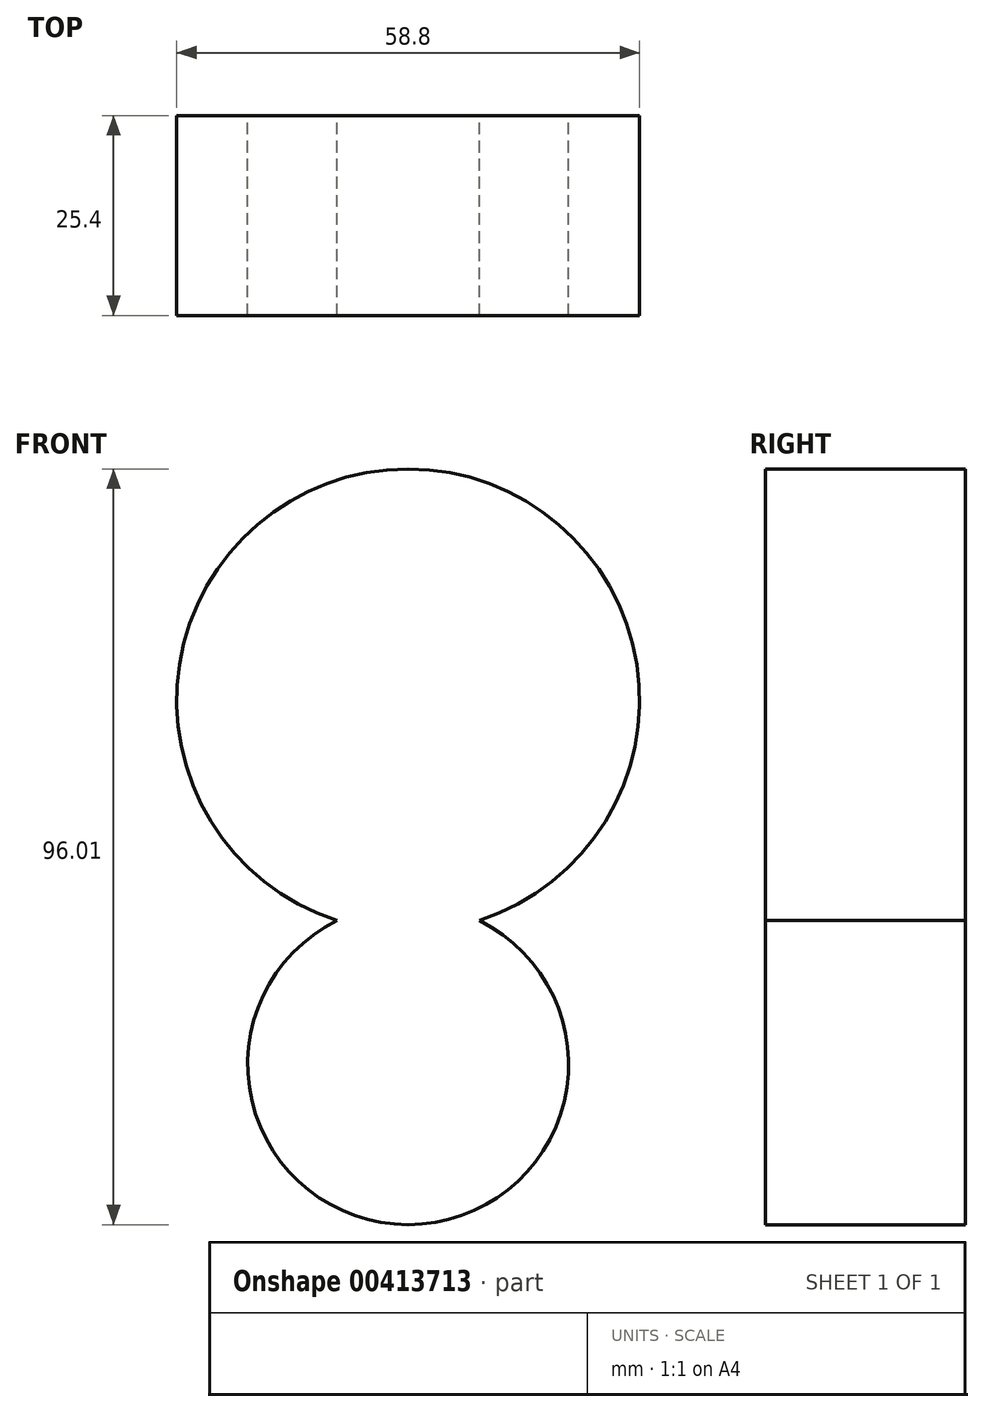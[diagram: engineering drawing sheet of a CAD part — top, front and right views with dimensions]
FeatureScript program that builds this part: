
annotation { "Feature Type Name" : "Feature", "Feature Type Description" : "" }
export const myFeature = defineFeature(function(context is Context, id is Id, definition is map)
    precondition{}
    {
        {
            var Q0;
            Q0=qCreatedBy(makeId("Front.planeOp"),FACE);
            var sketch = newSketch(context, id + "F0", { "sketchPlane" : qUnion([Q0])});
            skCircle(sketch, "E0", {"center": v(0, 0) * mm, "radius": 20.38 * mm});
            skSolve(sketch);
        }
        {
            var Q0;
            Q0=qSketchRegion(id+"F0",true);
            extrude(context, id + "F1", {"entities" : qUnion([Q0]), "depth" : 25.4 * mm});
        }
        {
            var Q0;
            Q0=qCreatedBy(makeId("Front.planeOp"),FACE);
            var sketch = newSketch(context, id + "F2", { "sketchPlane" : qUnion([Q0])});
            skCircle(sketch, "E1", {"center": v(0, 46.23) * mm, "radius": 29.4 * mm});
            skSolve(sketch);
        }
        {
            var Q0;
            Q0=qSketchRegion(id+"F2",true);
            extrude(context, id + "F3", {"entities" : qUnion([Q0]), "operationType" : NewBodyOperationType.ADD, "depth" : 25.4 * mm});
        }
        {
            var Q0;
            Q0=qCreatedBy(makeId("Front.planeOp"),FACE);
            var sketch = newSketch(context, id + "F4", { "sketchPlane" : qUnion([Q0])});
            skLineSegment(sketch, "E2", {"start": v(-219.82, 0) * mm, "end": v(-219.82, -38.5) * mm});
            skLineSegment(sketch, "E3", {"start": v(-219.82, -38.5) * mm, "end": v(-184, -38.5) * mm});
            skSolve(sketch);
        }
        {
            var Q0;
            Q0=qCreatedBy(makeId("Front.planeOp"),FACE);
            var sketch = newSketch(context, id + "F5", { "sketchPlane" : qUnion([Q0])});
            skLineSegment(sketch, "E4", {"start": v(-185.5, 0) * mm, "end": v(0, 0) * mm});
            skLineSegment(sketch, "E5", {"start": v(0, 0) * mm, "end": v(-185.5, 0) * mm});
            skLineSegment(sketch, "E6", {"start": v(-185.5, -35.53) * mm, "end": v(-185.5, 0) * mm});
            skLineSegment(sketch, "E7", {"start": v(-218.5, 0) * mm, "end": v(-185.5, 0) * mm});
            skSolve(sketch);
        }
        {
            var Q0;
            Q0=sQuery(id+"F5.wireOp",EDGE,"E6");
            var Q1;
            Q1=sQuery(id+"F4.wireOp",EDGE,"E3");
            var Q2;
            Q2=sQuery(id+"F4.wireOp",EDGE,"E2");
            var Q3;
            Q3=sQuery(id+"F5.wireOp",EDGE,"E7");
            extrude(context, id + "F6", {"bodyType" : ToolBodyType.SURFACE, "surfaceEntities" : qUnion([Q0, Q1, Q2, Q3]), "depth" : 115.12 * mm});
        }
        {
            var Q0;
            Q0=qCreatedBy(makeId("Front.planeOp"),FACE);
            var sketch = newSketch(context, id + "F7", { "sketchPlane" : qUnion([Q0])});
            skLineSegment(sketch, "E8", {"start": v(0, 0) * mm, "end": v(-186.4, 0) * mm});
            skSolve(sketch);
        }
        {
            var Q0;
            Q0=qSketchRegion(id+"F7",true);
            var Q1;
            Q1=sQuery(id+"F7.wireOp",EDGE,"E8");
            extrude(context, id + "F8", {"entities" : qUnion([Q0]), "bodyType" : ToolBodyType.SURFACE, "surfaceEntities" : qUnion([Q1]), "depth" : 37 * mm});
        }
    });
